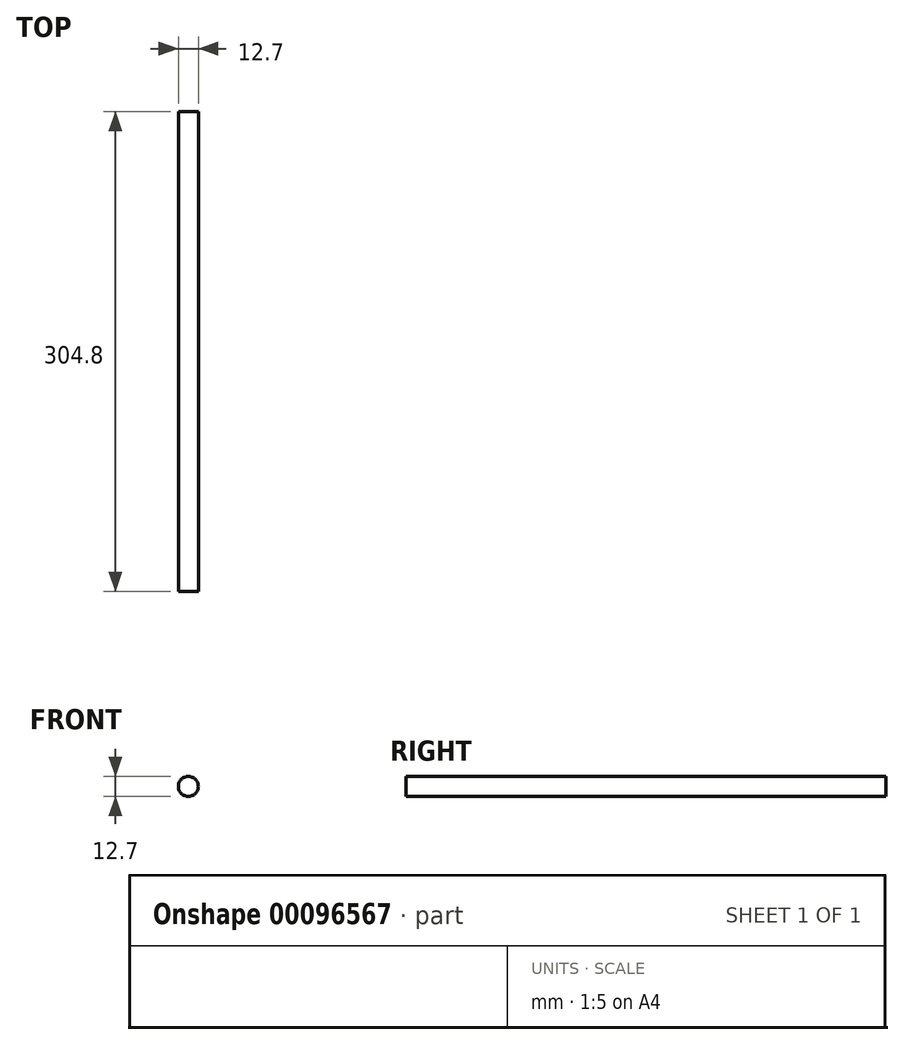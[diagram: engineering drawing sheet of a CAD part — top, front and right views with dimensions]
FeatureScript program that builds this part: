
annotation { "Feature Type Name" : "Feature", "Feature Type Description" : "" }
export const myFeature = defineFeature(function(context is Context, id is Id, definition is map)
    precondition{}
    {
        {
            var Q0;
            Q0=qCreatedBy(makeId("Front.planeOp"),FACE);
            var sketch = newSketch(context, id + "F0", { "sketchPlane" : qUnion([Q0])});
            skCircle(sketch, "E0", {"center": v(0, 0) * mm, "radius": 6.35 * mm});
            skSolve(sketch);
        }
        {
            var Q0;
            Q0 = qSketchRegion(id + "F0", true);
            extrude(context, id + "F1", {"entities" : qUnion([Q0]), "depth" : 304.8 * mm, "symmetric" : true});
        }
    });
